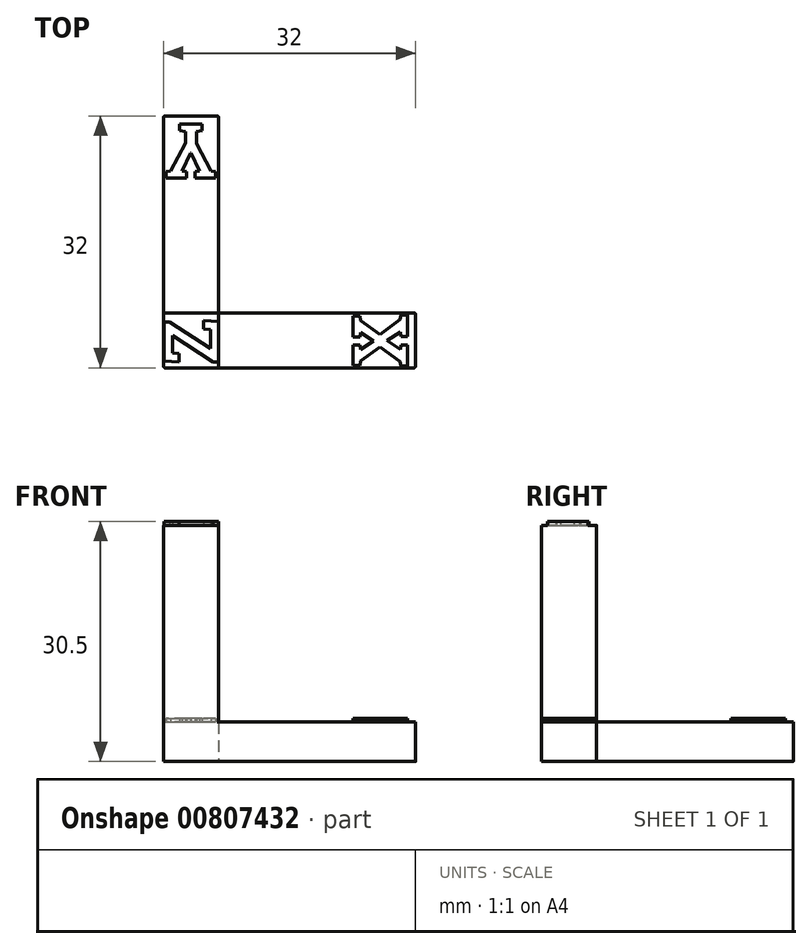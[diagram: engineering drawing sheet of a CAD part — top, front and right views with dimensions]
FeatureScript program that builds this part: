
annotation { "Feature Type Name" : "Feature", "Feature Type Description" : "" }
export const myFeature = defineFeature(function(context is Context, id is Id, definition is map)
    precondition{}
    {
        {
            var Q0;
            Q0=qCreatedBy(makeId("Top.planeOp"),FACE);
            var sketch = newSketch(context, id + "F0", { "sketchPlane" : qUnion([Q0])});
            skLineSegment(sketch, "E0", {"start": v(0, 32) * mm, "end": v(7, 32) * mm});
            skLineSegment(sketch, "E1", {"start": v(7, 32) * mm, "end": v(7, 7) * mm});
            skLineSegment(sketch, "E2", {"start": v(7, 7) * mm, "end": v(32, 7) * mm});
            skLineSegment(sketch, "E3", {"start": v(32, 7) * mm, "end": v(32, 0) * mm});
            skLineSegment(sketch, "E4", {"start": v(32, 0) * mm, "end": v(0, 0) * mm});
            skLineSegment(sketch, "E5", {"start": v(0, 0) * mm, "end": v(0, 32) * mm});
            skSolve(sketch);
        }
        {
            var Q0;
            Q0=makeQuery(id+"F0.imprint","IMPRINT",FACE,{"disambiguationData":[TD([[makeQuery(id+"F0.imprint","IMPRINT",EDGE,{"derivedFrom":sQuery(id+"F0.wireOp",EDGE,"E0")}),-1.0]])]});
            extrude(context, id + "F1", {"entities" : qUnion([Q0]), "depth" : 5 * mm, "offsetDistance" : 25 * mm});
        }
        {
            var Q0;
            Q0=makeQuery(id+"F1.opExtrude","CAP_FACE",FACE,{"disambiguationData":[OSD([sQuery(id+"F0.wireOp",EDGE,"E0"),sQuery(id+"F0.wireOp",EDGE,"E1"),sQuery(id+"F0.wireOp",EDGE,"E2"),sQuery(id+"F0.wireOp",EDGE,"E3"),sQuery(id+"F0.wireOp",EDGE,"E4"),sQuery(id+"F0.wireOp",EDGE,"E5")])],"isStart":true});
            var sketch = newSketch(context, id + "F2", { "sketchPlane" : qUnion([Q0])});
            skLineSegment(sketch, "E6.bottom", {"start": v(7, -7) * mm, "end": v(0, -7) * mm});
            skLineSegment(sketch, "E6.top", {"start": v(7, 0) * mm, "end": v(0, 0) * mm});
            skLineSegment(sketch, "E6.left", {"start": v(7, -7) * mm, "end": v(7, 0) * mm});
            skLineSegment(sketch, "E6.right", {"start": v(0, -7) * mm, "end": v(0, 0) * mm});
            skSolve(sketch);
        }
        {
            var Q0;
            Q0=makeQuery(id+"F2.imprint","IMPRINT",FACE,{"disambiguationData":[TD([[makeQuery(id+"F2.imprint","IMPRINT",EDGE,{"derivedFrom":sQuery(id+"F2.wireOp",EDGE,"E6.bottom")}),-1.0]])]});
            extrude(context, id + "F3", {"entities" : qUnion([Q0]), "operationType" : NewBodyOperationType.ADD, "oppositeDirection" : true, "depth" : 30 * mm, "offsetDistance" : 25 * mm});
        }
        {
            var Q0;
            {var subQ0=sQuery(id+"F0.wireOp",EDGE,"E3");var subQ1=sQuery(id+"F0.wireOp",EDGE,"E2");var subQ2=sQuery(id+"F0.wireOp",EDGE,"E1");var subQ3=sQuery(id+"F0.wireOp",EDGE,"E4");var subQ4=makeQuery(id+"F1.opExtrude","CAP_FACE",FACE,{"disambiguationData":[OSD([sQuery(id+"F0.wireOp",EDGE,"E0"),subQ2,subQ1,subQ0,subQ3,sQuery(id+"F0.wireOp",EDGE,"E5")])],"isStart":false});Q0=makeQuery(id+"F3.boolean.opBoolean","SPLIT",FACE,{"disambiguationData":[TD([makeQuery(id+"F1.opExtrude","SWEPT_FACE",FACE,{"disambiguationData":[OSD([subQ0])]})])],"derivedFrom":subQ4});}
            var sketch = newSketch(context, id + "F4", { "sketchPlane" : qUnion([Q0])});
            skText(sketch, "E7", { "text": "X", "fontName": "RobotoSlab-Bold.ttf"});
            const initialGuessF4  = {"E7": [0.031, 7e-05, 0, 1, 0.007]};
            skSetInitialGuess(sketch, initialGuessF4);
            skSolve(sketch);
        }
        {
            var Q0;
            Q0 = qSketchRegion(id + "F4", true);
            extrude(context, id + "F5", {"entities" : qUnion([Q0]), "operationType" : NewBodyOperationType.ADD, "depth" : .5 * mm, "offsetDistance" : 25 * mm});
        }
        {
            var Q0;
            {var subQ0=sQuery(id+"F0.wireOp",EDGE,"E2");var subQ1=sQuery(id+"F0.wireOp",EDGE,"E1");var subQ2=sQuery(id+"F0.wireOp",EDGE,"E5");var subQ3=sQuery(id+"F0.wireOp",EDGE,"E0");var subQ4=makeQuery(id+"F1.opExtrude","CAP_FACE",FACE,{"disambiguationData":[OSD([subQ3,subQ1,subQ0,sQuery(id+"F0.wireOp",EDGE,"E3"),sQuery(id+"F0.wireOp",EDGE,"E4"),subQ2])],"isStart":false});Q0=makeQuery(id+"F3.boolean.opBoolean","SPLIT",FACE,{"disambiguationData":[TD([makeQuery(id+"F1.opExtrude","SWEPT_FACE",FACE,{"disambiguationData":[OSD([subQ3])]})])],"derivedFrom":subQ4});}
            var sketch = newSketch(context, id + "F6", { "sketchPlane" : qUnion([Q0])});
            skText(sketch, "E8", { "text": "Y", "fontName": "RobotoSlab-Bold.ttf"});
            skPoint(sketch, "E9", {"position": v(3.23, 32.4) * mm});
            const initialGuessF6  = {"E8": [0.00676, 0.031, -1, 0, 0.007]};
            skSetInitialGuess(sketch, initialGuessF6);
            skSolve(sketch);
        }
        {
            var Q0;
            Q0=makeQuery(id+"F6.imprint","IMPRINT",FACE,{"disambiguationData":[TD([[makeQuery(id+"F6.imprint","IMPRINT",EDGE,{"derivedFrom":sQuery(id+"F6.wireOp",EDGE,"E8.sketch_text.stroke-0")}),-1.0]])]});
            extrude(context, id + "F7", {"entities" : qUnion([Q0]), "operationType" : NewBodyOperationType.ADD, "depth" : .5 * mm, "offsetDistance" : 25 * mm});
        }
        {
            var Q0;
            Q0=makeQuery(id+"F3.opExtrude","CAP_FACE",FACE,{"disambiguationData":[OSD([sQuery(id+"F2.wireOp",EDGE,"E6.bottom"),sQuery(id+"F2.wireOp",EDGE,"E6.top"),sQuery(id+"F2.wireOp",EDGE,"E6.left"),sQuery(id+"F2.wireOp",EDGE,"E6.right")])],"isStart":false});
            var sketch = newSketch(context, id + "F8", { "sketchPlane" : qUnion([Q0])});
            skText(sketch, "E10", { "text": "Z", "fontName": "RobotoSlab-Bold.ttf"});
            skPoint(sketch, "E11", {"position": v(2.65, 38.82) * mm});
            const initialGuessF8  = {"E10": [0.007, 0.0004, 0, 1, 0.007]};
            skSetInitialGuess(sketch, initialGuessF8);
            skSolve(sketch);
        }
        {
            var Q0;
            Q0 = qSketchRegion(id + "F8", true);
            extrude(context, id + "F9", {"entities" : qUnion([Q0]), "operationType" : NewBodyOperationType.ADD, "depth" : .5 * mm, "offsetDistance" : 25 * mm});
        }
        {
            var Q0;
            Q0=makeQuery(id+"F1.opExtrude","SWEPT_EDGE",EDGE,{"disambiguationData":[OSD([sQuery(id+"F0.wireOp",EDGE,"E2"),sQuery(id+"F0.wireOp",EDGE,"E3")])]});
            var Q1;
            Q1=makeQuery(id+"F1.opExtrude","SWEPT_EDGE",EDGE,{"disambiguationData":[OSD([sQuery(id+"F0.wireOp",EDGE,"E3"),sQuery(id+"F0.wireOp",EDGE,"E4")])]});
            var Q2;
            Q2=makeQuery(id+"F1.opExtrude","SWEPT_EDGE",EDGE,{"disambiguationData":[OSD([sQuery(id+"F0.wireOp",EDGE,"E1"),sQuery(id+"F0.wireOp",EDGE,"E2")])]});
            var Q3;
            Q3=makeQuery(id+"F1.opExtrude","SWEPT_EDGE",EDGE,{"disambiguationData":[OSD([sQuery(id+"F0.wireOp",EDGE,"E0"),sQuery(id+"F0.wireOp",EDGE,"E1")])]});
            var Q4;
            Q4=makeQuery(id+"F1.opExtrude","SWEPT_EDGE",EDGE,{"disambiguationData":[OSD([sQuery(id+"F0.wireOp",EDGE,"E0"),sQuery(id+"F0.wireOp",EDGE,"E5")])]});
            var Q5;
            Q5=makeQuery(id+"F3.boolean.opBoolean","MERGE",EDGE,{"derivedFrom":[makeQuery(id+"F1.opExtrude","SWEPT_EDGE",EDGE,{"disambiguationData":[OSD([sQuery(id+"F0.wireOp",EDGE,"E4"),sQuery(id+"F0.wireOp",EDGE,"E5")])]}),makeQuery(id+"F3.opExtrude","SWEPT_EDGE",EDGE,{"disambiguationData":[OSD([sQuery(id+"F2.wireOp",EDGE,"E6.top"),sQuery(id+"F2.wireOp",EDGE,"E6.right")])]})]});
            var Q6;
            Q6=makeQuery(id+"F3.opExtrude","SWEPT_EDGE",EDGE,{"disambiguationData":[OSD([sQuery(id+"F0.wireOp",EDGE,"E4"),sQuery(id+"F2.wireOp",EDGE,"E6.top"),sQuery(id+"F2.wireOp",EDGE,"E6.left")])]});
            var Q7;
            Q7=makeQuery(id+"F3.opExtrude","SWEPT_EDGE",EDGE,{"disambiguationData":[OSD([sQuery(id+"F0.wireOp",EDGE,"E5"),sQuery(id+"F2.wireOp",EDGE,"E6.bottom"),sQuery(id+"F2.wireOp",EDGE,"E6.right")])]});
            fillet(context, id + "F10", {"entities" : qUnion([Q0, Q1, Q2, Q3, Q4, Q5, Q6, Q7]), "radius" : 0.2 * mm, "allowEdgeOverflow" : false});
        }
        {
            var Q0;
            Q0=makeQuery(id+"F3.opExtrude","SWEPT_EDGE",EDGE,{"disambiguationData":[OSD([sQuery(id+"F0.wireOp",EDGE,"E1"),sQuery(id+"F0.wireOp",EDGE,"E2"),sQuery(id+"F2.wireOp",EDGE,"E6.bottom"),sQuery(id+"F2.wireOp",EDGE,"E6.left")])]});
            fillet(context, id + "F11", {"entities" : qUnion([Q0]), "radius" : 0.2 * mm, "tangentPropagation" : true, "allowEdgeOverflow" : false});
        }
    });
